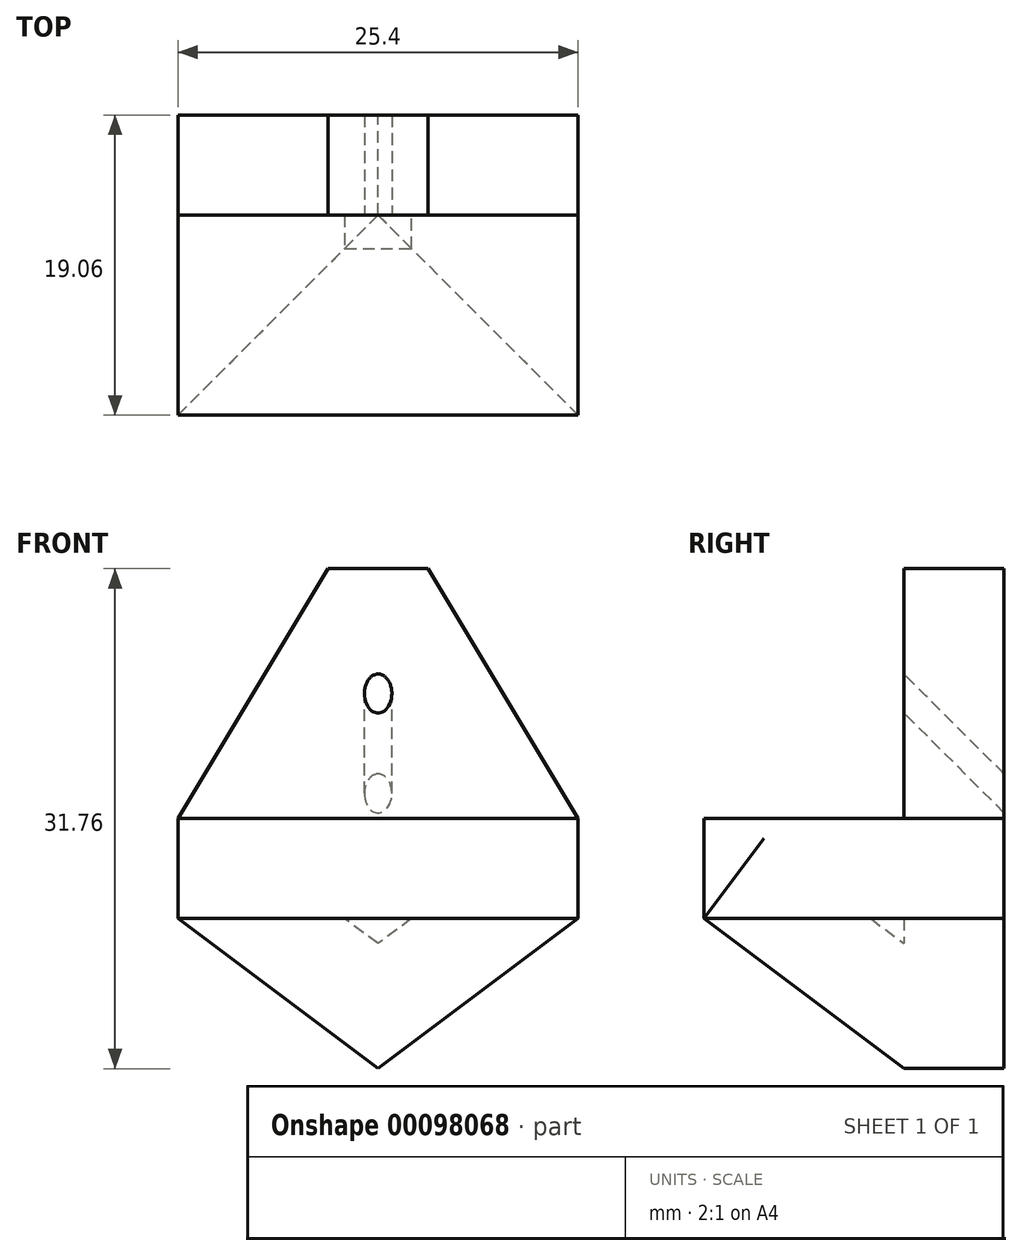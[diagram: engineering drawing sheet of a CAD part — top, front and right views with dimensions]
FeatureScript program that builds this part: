
annotation { "Feature Type Name" : "Feature", "Feature Type Description" : "" }
export const myFeature = defineFeature(function(context is Context, id is Id, definition is map)
    precondition{}
    {
        {
            var Q0;
            Q0=qCreatedBy(makeId("Front.planeOp"),FACE);
            var sketch = newSketch(context, id + "F0", { "sketchPlane" : qUnion([Q0])});
            skLineSegment(sketch, "E0", {"start": v(0, 15.88) * mm, "end": v(3.18, 15.88) * mm});
            skLineSegment(sketch, "E1", {"start": v(3.18, 15.88) * mm, "end": v(12.7, 0) * mm});
            skLineSegment(sketch, "E2", {"start": v(12.7, 0) * mm, "end": v(12.7, -6.35) * mm});
            skLineSegment(sketch, "E3", {"start": v(12.7, -6.35) * mm, "end": v(0, -15.88) * mm});
            skLineSegment(sketch, "E4.MirrorCS", {"start": v(-12.7, -6.35) * mm, "end": v(0, -15.88) * mm});
            skLineSegment(sketch, "E5.MirrorCS", {"start": v(-12.7, 0) * mm, "end": v(-12.7, -6.35) * mm});
            skLineSegment(sketch, "E6.MirrorCS", {"start": v(0, 15.88) * mm, "end": v(-3.17, 15.88) * mm});
            skLineSegment(sketch, "E7.MirrorCS", {"start": v(-3.18, 15.88) * mm, "end": v(-12.7, 0) * mm});
            skLineSegment(sketch, "E8", {"start": v(-12.7, 0) * mm, "end": v(12.7, 0) * mm});
            skLineSegment(sketch, "E9", {"start": v(-12.7, -6.35) * mm, "end": v(12.7, -6.35) * mm});
            skLineSegment(sketch, "E10", {"start": v(0, -6.35) * mm, "end": v(0, -15.88) * mm});
            skLineSegment(sketch, "E11", {"start": v(0, 15.88) * mm, "end": v(0, 9.52) * mm, "construction": true});
            skLineSegment(sketch, "E12", {"start": v(0, 9.52) * mm, "end": v(-2.21, 9.52) * mm, "construction": true});
            skSolve(sketch);
        }
        {
            var Q0;
            Q0 = qSketchRegion(id + "F0", true);
            extrude(context, id + "F1", {"entities" : qUnion([Q0]), "endBound" : BoundingType.SYMMETRIC, "depth" : 6.35 * mm});
        }
        {
            var Q0;
            Q0=makeQuery(id+"F1.opExtrude","CAP_FACE",FACE,{"disambiguationData":[OSD([sQuery(id+"F0.wireOp",EDGE,"E0"),sQuery(id+"F0.wireOp",EDGE,"E1"),sQuery(id+"F0.wireOp",EDGE,"E2"),sQuery(id+"F0.wireOp",EDGE,"E3"),sQuery(id+"F0.wireOp",EDGE,"E4.MirrorCS"),sQuery(id+"F0.wireOp",EDGE,"E5.MirrorCS"),sQuery(id+"F0.wireOp",EDGE,"E6.MirrorCS"),sQuery(id+"F0.wireOp",EDGE,"E7.MirrorCS")])],"isStart":false});
            var sketch = newSketch(context, id + "F2", { "sketchPlane" : qUnion([Q0])});
            skLineSegment(sketch, "E13", {"start": v(-12.7, 0) * mm, "end": v(-12.7, -6.35) * mm});
            skLineSegment(sketch, "E14", {"start": v(-12.7, -6.35) * mm, "end": v(12.7, -6.35) * mm});
            skLineSegment(sketch, "E15", {"start": v(12.7, -6.35) * mm, "end": v(12.7, 0) * mm});
            skLineSegment(sketch, "E16", {"start": v(12.7, 0) * mm, "end": v(-12.7, 0) * mm});
            skSolve(sketch);
        }
        {
            var Q0;
            Q0 = qSketchRegion(id + "F2", true);
            extrude(context, id + "F3", {"entities" : qUnion([Q0]), "operationType" : NewBodyOperationType.ADD, "depth" : 12.7 * mm});
        }
        {
            var Q0;
            Q0=makeQuery(id+"F1.opExtrude","SWEPT_FACE",FACE,{"disambiguationData":[OSD([sQuery(id+"F0.wireOp",EDGE,"E3")])]});
            var sketch = newSketch(context, id + "F4", { "sketchPlane" : qUnion([Q0])});
            skLineSegment(sketch, "E17", {"start": v(6.35, 3.18) * mm, "end": v(6.35, 15.88) * mm});
            skLineSegment(sketch, "E18", {"start": v(6.35, 3.18) * mm, "end": v(-9.53, 3.18) * mm});
            skLineSegment(sketch, "E19", {"start": v(-9.53, 3.17) * mm, "end": v(6.35, 15.88) * mm});
            skSolve(sketch);
        }
        {
            var Q0;
            Q0 = qSketchRegion(id + "F4", true);
            extrude(context, id + "F5", {"entities" : qUnion([Q0]), "operationType" : NewBodyOperationType.ADD, "oppositeDirection" : true, "depth" : 6.35 * mm});
        }
        {
            var Q0;
            Q0=makeQuery(id+"F1.opExtrude","SWEPT_FACE",FACE,{"disambiguationData":[OSD([sQuery(id+"F0.wireOp",EDGE,"E4.MirrorCS")])]});
            var sketch = newSketch(context, id + "F6", { "sketchPlane" : qUnion([Q0])});
            skLineSegment(sketch, "E20", {"start": v(-6.35, 3.18) * mm, "end": v(-6.35, 15.88) * mm});
            skLineSegment(sketch, "E21", {"start": v(-6.35, 3.18) * mm, "end": v(9.53, 3.18) * mm});
            skLineSegment(sketch, "E22", {"start": v(9.53, 3.17) * mm, "end": v(-6.35, 15.88) * mm});
            skSolve(sketch);
        }
        {
            var Q0;
            Q0 = qSketchRegion(id + "F6", true);
            extrude(context, id + "F7", {"entities" : qUnion([Q0]), "operationType" : NewBodyOperationType.ADD, "oppositeDirection" : true, "depth" : 6.35 * mm});
        }
        {
            var Q0;
            Q0=makeQuery(id+"F7.boolean.opBoolean","MERGE",VERTEX,{"derivedFrom":[makeQuery(id+"F3.opExtrude","CAP_VERTEX",VERTEX,{"disambiguationData":[OSD([sQuery(id+"F0.wireOp",EDGE,"E4.MirrorCS"),sQuery(id+"F2.wireOp",EDGE,"E13"),sQuery(id+"F2.wireOp",EDGE,"E14")])],"isStart":false}),makeQuery(id+"F7.opExtrude","CAP_VERTEX",VERTEX,{"disambiguationData":[OSD([sQuery(id+"F6.wireOp",EDGE,"E20"),sQuery(id+"F6.wireOp",EDGE,"E22")])],"isStart":true})]});
            var Q1;
            Q1=makeQuery(id+"F5.boolean.opBoolean","MERGE",VERTEX,{"derivedFrom":[makeQuery(id+"F3.opExtrude","CAP_VERTEX",VERTEX,{"disambiguationData":[OSD([sQuery(id+"F0.wireOp",EDGE,"E3"),sQuery(id+"F2.wireOp",EDGE,"E14"),sQuery(id+"F2.wireOp",EDGE,"E15")])],"isStart":false}),makeQuery(id+"F5.opExtrude","CAP_VERTEX",VERTEX,{"disambiguationData":[OSD([sQuery(id+"F4.wireOp",EDGE,"E17"),sQuery(id+"F4.wireOp",EDGE,"E19")])],"isStart":true})]});
            var Q2;
            {var subQ0=sQuery(id+"F0.wireOp",EDGE,"E10");var subQ1=sQuery(id+"F0.wireOp",EDGE,"E4.MirrorCS");var subQ2=sQuery(id+"F0.wireOp",EDGE,"E3");Q2=makeQuery(id+"F7.boolean.opBoolean","MERGE",VERTEX,{"derivedFrom":[makeQuery(id+"F5.boolean.opBoolean","MERGE",VERTEX,{"derivedFrom":[makeQuery(id+"F1.opExtrude","CAP_VERTEX",VERTEX,{"disambiguationData":[OSD([subQ2,subQ1,subQ0])],"isStart":false}),makeQuery(id+"F5.opExtrude","CAP_VERTEX",VERTEX,{"disambiguationData":[OSD([subQ2,subQ1,subQ0,sQuery(id+"F4.wireOp",EDGE,"E18"),sQuery(id+"F4.wireOp",EDGE,"E19")])],"isStart":true})]}),makeQuery(id+"F7.opExtrude","CAP_VERTEX",VERTEX,{"disambiguationData":[OSD([subQ2,subQ1,subQ0,sQuery(id+"F6.wireOp",EDGE,"E21"),sQuery(id+"F6.wireOp",EDGE,"E22")])],"isStart":true})]});}
            cPlane(context, id + "F8", {"entities" : qUnion([Q0, Q1, Q2]), "cplaneType" : CPlaneType.THREE_POINT, "offset" : 152.4 * mm, "width" : 152.4 * mm, "height" : 152.4 * mm});
        }
        {
            var Q0;
            Q0=qCreatedBy(id+"F8.planeOp",FACE);
            var sketch = newSketch(context, id + "F9", { "sketchPlane" : qUnion([Q0])});
            skLineSegment(sketch, "E23", {"start": v(12.7, 8.89) * mm, "end": v(-12.7, 8.89) * mm});
            skLineSegment(sketch, "E24", {"start": v(-12.7, 8.89) * mm, "end": v(0, -6.99) * mm});
            skLineSegment(sketch, "E25", {"start": v(0, -6.99) * mm, "end": v(12.7, 8.89) * mm});
            skSolve(sketch);
        }
        {
            var Q0;
            Q0 = qSketchRegion(id + "F9", true);
            extrude(context, id + "F10", {"entities" : qUnion([Q0]), "operationType" : NewBodyOperationType.ADD, "oppositeDirection" : true, "depth" : 6.35 * mm});
        }
        {
            var Q0;
            Q0=makeQuery(id+"F3.opExtrude","SWEPT_FACE",FACE,{"disambiguationData":[OSD([sQuery(id+"F2.wireOp",EDGE,"E16")])]});
            var sketch = newSketch(context, id + "F11", { "sketchPlane" : qUnion([Q0])});
            skLineSegment(sketch, "E26", {"start": v(-12.7, -15.88) * mm, "end": v(-12.7, -19.05) * mm});
            skSolve(sketch);
        }
        {
            var Q0;
            Q0=sQuery(id+"F11.wireOp",VERTEX,"E26.end");
            var Q1;
            Q1=makeQuery(id+"F1.opExtrude","CAP_VERTEX",VERTEX,{"disambiguationData":[OSD([sQuery(id+"F0.wireOp",EDGE,"E6.MirrorCS"),sQuery(id+"F0.wireOp",EDGE,"E7.MirrorCS")])],"isStart":false});
            var Q2;
            Q2=makeQuery(id+"F1.opExtrude","CAP_VERTEX",VERTEX,{"disambiguationData":[OSD([sQuery(id+"F0.wireOp",EDGE,"E0"),sQuery(id+"F0.wireOp",EDGE,"E1")])],"isStart":false});
            cPlane(context, id + "F12", {"entities" : qUnion([Q0, Q1, Q2]), "cplaneType" : CPlaneType.THREE_POINT, "offset" : 152.4 * mm, "width" : 152.4 * mm, "height" : 152.4 * mm});
        }
        {
            var Q0;
            Q0=qCreatedBy(id+"F12.planeOp",FACE);
            var sketch = newSketch(context, id + "F13", { "sketchPlane" : qUnion([Q0])});
            skLineSegment(sketch, "E27", {"start": v(0, 3.38) * mm, "end": v(0, 5.92) * mm, "construction": true});
            skCircle(sketch, "E28", {"center": v(0, 3.38) * mm, "radius": 0.87 * mm});
            skSolve(sketch);
        }
        {
            var Q0;
            Q0 = qSketchRegion(id + "F13", true);
            extrude(context, id + "F14", {"entities" : qUnion([Q0]), "operationType" : NewBodyOperationType.REMOVE, "oppositeDirection" : true, "depth" : 25.4 * mm});
        }
    });
